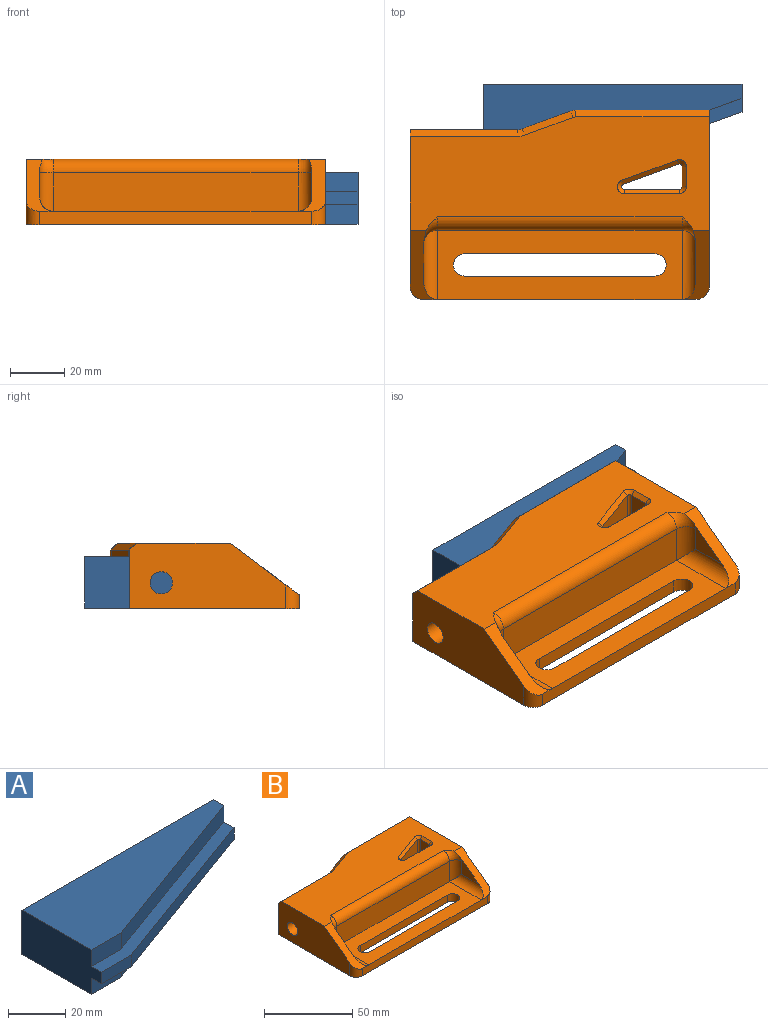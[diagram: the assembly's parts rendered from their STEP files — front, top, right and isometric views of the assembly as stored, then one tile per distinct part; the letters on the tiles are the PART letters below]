
ASSEMBLY  parts=2 mates=2
PART A: 13 faces, bbox 95x39.2x19.1 mm
  f0: plane 15x7.03mm, normal (0,-1,0), area 105.4mm2, adj f1,f2,f7,f10
  f1: plane 80x29.12mm, normal (0.34,-0.94,0), area 598.1mm2, adj f0,f5,f7,f10
  f2: plane 39.21x19.05mm, normal (-1,0,0), area 676.7mm2, adj f0,f3,f6,f7,f8,f9,f10,f11
  f3: plane 15x7.03mm, normal (0,-1,0), area 105.4mm2, adj f2,f4,f8,f11
  f4: plane 80x29.12mm, normal (0.34,-0.94,0), area 598.1mm2, adj f3,f5,f8,f11
  f5: plane 19.05x10.09mm, normal (1,0,0), area 122mm2, adj f1,f4,f6,f7,f8,f10,f11,f12
  f6: plane 95x19.05mm, normal (0,1,0), area 1809.8mm2, adj f2,f5,f7,f8
  f7: plane 95x34.21mm, normal (0,0,1), area 2085.4mm2, adj f0,f1,f2,f5,f6
  f8: plane 95x34.21mm, normal (0,0,-1), area 2085.4mm2, adj f2,f3,f4,f5,f6
  f9: plane 15x5mm, normal (0,-1,0), area 75mm2, adj f2,f10,f11,f12
  f10: plane 95x34.12mm, normal (0,0,1), area 475mm2, adj f0,f1,f2,f5,f9,f12
  f11: plane 95x34.12mm, normal (0,0,-1), area 475mm2, adj f2,f3,f4,f5,f9,f12
  f12: plane 80x29.12mm, normal (0.34,-0.94,0), area 425.7mm2, adj f5,f9,f10,f11
PART B: 64 faces, bbox 110.5x70.1x34.3 mm
  f0: cylinder r=5mm len=2.25mm, axis (0,0,-1), area 3.9mm2, adj f11,f20,f55,f63
  f1: plane 110x69.52mm, normal (0,0,-1), area 5174.2mm2, adj f7,f8,f9,f10,f11,f12,f14,f15
  f2: plane 110.54x42.16mm, normal (0,0,1), area 3526.7mm2, adj f7,f12,f21,f23,f34,f37,f40,f47
  f3: plane 90x14.05mm, normal (0,-1,0), area 1264.5mm2, adj f4,f34,f36,f39
  f4: plane 90x25.4mm, normal (0,0,1), area 1660.2mm2, adj f3,f14,f15,f16,f17,f18,f35,f38
  f5: plane 80x29.12mm, normal (-0.34,0.94,0), area 602.3mm2, adj f6,f7,f62,f63
  f6: plane 15x7.08mm, normal (0,1,0), area 106.1mm2, adj f5,f10,f62,f63
  f7: plane 64.52x24.05mm, normal (1,0,0), area 1362.6mm2, adj f1,f2,f5,f8,f19,f21,f32,f58
  f8: plane 80x29.12mm, normal (-0.34,0.94,0), area 581mm2, adj f1,f7,f9,f61
  f9: plane 15x6.83mm, normal (0,1,0), area 102.4mm2, adj f1,f8,f10,f61
  f10: plane 27.5x19.3mm, normal (1,0,0), area 309.1mm2, adj f1,f6,f9,f11,f26,f27,f28,f29
  f11: plane 39.52x21.55mm, normal (0,1,0), area 378.4mm2, adj f0,f1,f10,f12,f54,f63
  f12: plane 57.4x24.05mm, normal (-1,0,0), area 1168.6mm2, adj f1,f2,f11,f13,f23,f33,f54
  f13: cylinder r=4.09mm len=8.19mm, axis (-1,0,0), area 205.8mm2, adj f12,f25
  f14: cylinder r=4.09mm len=8.19mm, axis (0,0,-1), area 64.3mm2, adj f1,f4,f15,f18
  f15: plane 70x5mm, normal (0,1,0), area 350mm2, adj f1,f4,f14,f16
  f16: cylinder r=4.09mm len=8.19mm, axis (0,0,-1), area 64.3mm2, adj f1,f4,f15,f18
  f17: plane 100x5mm, normal (0,-1,0), area 500mm2, adj f1,f4,f21,f23,f32,f33
  f18: plane 70x5mm, normal (0,-1,0), area 350mm2, adj f1,f4,f14,f16
  f19: plane 49.16x2.25mm, normal (0,1,0), area 110.6mm2, adj f7,f53,f58,f63
  f20: plane 17.9x6.51mm, normal (-0.34,0.94,0), area 42.9mm2, adj f0,f53,f56,f63
  f21: plane 25.4x19.05mm, normal (0,-0.6,0.8), area 163.5mm2, adj f2,f7,f17,f22,f32,f35,f37
  f22: plane 13.82x10.37mm, normal (-1,0,0), area 70.8mm2, adj f21,f35,f36,f37
  f23: plane 25.4x19.05mm, normal (0,-0.6,0.8), area 163.5mm2, adj f2,f12,f17,f24,f33,f38,f40
  f24: plane 13.82x10.37mm, normal (1,0,0), area 70.8mm2, adj f23,f38,f39,f40
  f25: plane 14.95x12.95mm, normal (1,0,0), area 92.6mm2, adj f13,f26,f27,f28,f29,f30,f31
  f26: plane 7x6.48mm, normal (0,0.87,0.5), area 52.3mm2, adj f10,f25,f27,f30
  f27: plane 7x6.48mm, normal (0,0.87,-0.5), area 52.3mm2, adj f10,f25,f26,f28
  f28: plane 7.48x7mm, normal (0,0,-1), area 52.3mm2, adj f10,f25,f27,f29
  f29: plane 7x6.48mm, normal (0,-0.87,-0.5), area 52.3mm2, adj f10,f25,f28,f31
  f30: plane 7.48x7mm, normal (0,0,1), area 52.3mm2, adj f10,f25,f26,f31
  f31: plane 7x6.48mm, normal (0,-0.87,0.5), area 52.3mm2, adj f10,f25,f29,f30
  f32: cylinder r=5mm len=8.75mm, axis (0,0,-1), area 50mm2, adj f1,f7,f17,f21
  f33: cylinder r=5mm len=8.75mm, axis (0,0,-1), area 50mm2, adj f1,f12,f17,f23
  f34: cylinder r=5mm len=90mm, axis (-1,0,0), area 706.9mm2, adj f2,f3,f37,f40
  f35: cylinder r=5mm len=25.4mm, axis (0,1,0), area 166.2mm2, adj f4,f21,f22,f36
  f36: cylinder r=5mm len=14.05mm, axis (0,0,1), area 96.1mm2, adj f3,f22,f35,f37
  f37: torus R=10mm, axis (1,0,0), area 40.4mm2, adj f2,f21,f22,f34,f36
  f38: cylinder r=5mm len=25.4mm, axis (0,1,0), area 166.2mm2, adj f4,f23,f24,f39
  f39: cylinder r=5mm len=14.05mm, axis (0,0,1), area 96.1mm2, adj f3,f24,f38,f40
  f40: torus R=10mm, axis (-1,0,0), area 40.4mm2, adj f2,f23,f24,f34,f39
  f41: plane 22.55x7.41mm, normal (-1,0,0), area 167.1mm2, adj f1,f44,f46,f50
  f42: plane 22.55x20.35mm, normal (0.34,-0.94,0), area 488.4mm2, adj f1,f44,f45,f47
  f43: plane 22.55x20.35mm, normal (0,1,0), area 459mm2, adj f1,f45,f46,f51
  f44: cylinder r=1mm len=22.55mm, axis (0,0,-1), area 43.3mm2, adj f1,f41,f42,f48
  f45: cylinder r=1mm len=22.55mm, axis (0,0,-1), area 63mm2, adj f1,f42,f43,f49
  f46: cylinder r=1mm len=22.55mm, axis (0,0,-1), area 35.4mm2, adj f1,f41,f43,f52
  f47: plane 20.87x8.82mm, normal (0.24,-0.66,0.71), area 45.9mm2, adj f2,f42,f48,f49
  f48: cone r=2.5mm half-angle=45deg, axis (0,0,1), area 7.1mm2, adj f2,f44,f47,f50
  f49: cone r=2.5mm half-angle=45deg, axis (0,0,1), area 10.4mm2, adj f2,f45,f47,f51
  f50: plane 7.41x1.5mm, normal (-0.71,0,0.71), area 15.7mm2, adj f2,f41,f48,f52
  f51: plane 20.35x1.5mm, normal (0,0.71,0.71), area 43.2mm2, adj f2,f43,f49,f52
  f52: cone r=2.5mm half-angle=45deg, axis (0,0,1), area 5.8mm2, adj f2,f46,f50,f51
  f53: cylinder r=5mm len=2.25mm, axis (0,0,-1), area 3.9mm2, adj f19,f20,f57,f63
  f54: plane 39.52x2.5mm, normal (0,0.71,0.71), area 139.7mm2, adj f2,f11,f12,f55
  f55: cone r=7.5mm half-angle=45deg, axis (0,0,1), area 7.7mm2, adj f0,f2,f54,f56
  f56: plane 18.75x8.86mm, normal (-0.24,0.66,0.71), area 67.3mm2, adj f2,f20,f55,f57
  f57: cone r=2.5mm half-angle=45deg, axis (0,0,-1), area 4.6mm2, adj f2,f53,f56,f58
  f58: plane 49.16x2.5mm, normal (0,0.71,0.71), area 173.8mm2, adj f2,f7,f19,f57
  f59: plane 79.91x29.09mm, normal (-0.34,0.94,0), area 459.2mm2, adj f7,f60,f61,f62
  f60: plane 15.09x5.4mm, normal (0,1,0), area 81.5mm2, adj f10,f59,f61,f62
  f61: plane 95x34.62mm, normal (0,0,1), area 525.1mm2, adj f7,f8,f9,f10,f59,f60
  f62: plane 95x34.62mm, normal (0,0,-1), area 525.1mm2, adj f5,f6,f7,f10,f59,f60
  f63: plane 95x29.12mm, normal (0,0,-1), area 1351.1mm2, adj f0,f5,f6,f10,f11,f19,f20,f53
PLACE A t=(11.98,4.36,0.25)mm
PLACE B at identity fixed
MATE planar A.f7 <-> B.f63  axis (0,0,1) through (7.84,40.6,9.78)mm
MATE planar B.f5 <-> A.f4  axis (-0.34,0.94,0) through (15,29.56,6.24)mm
